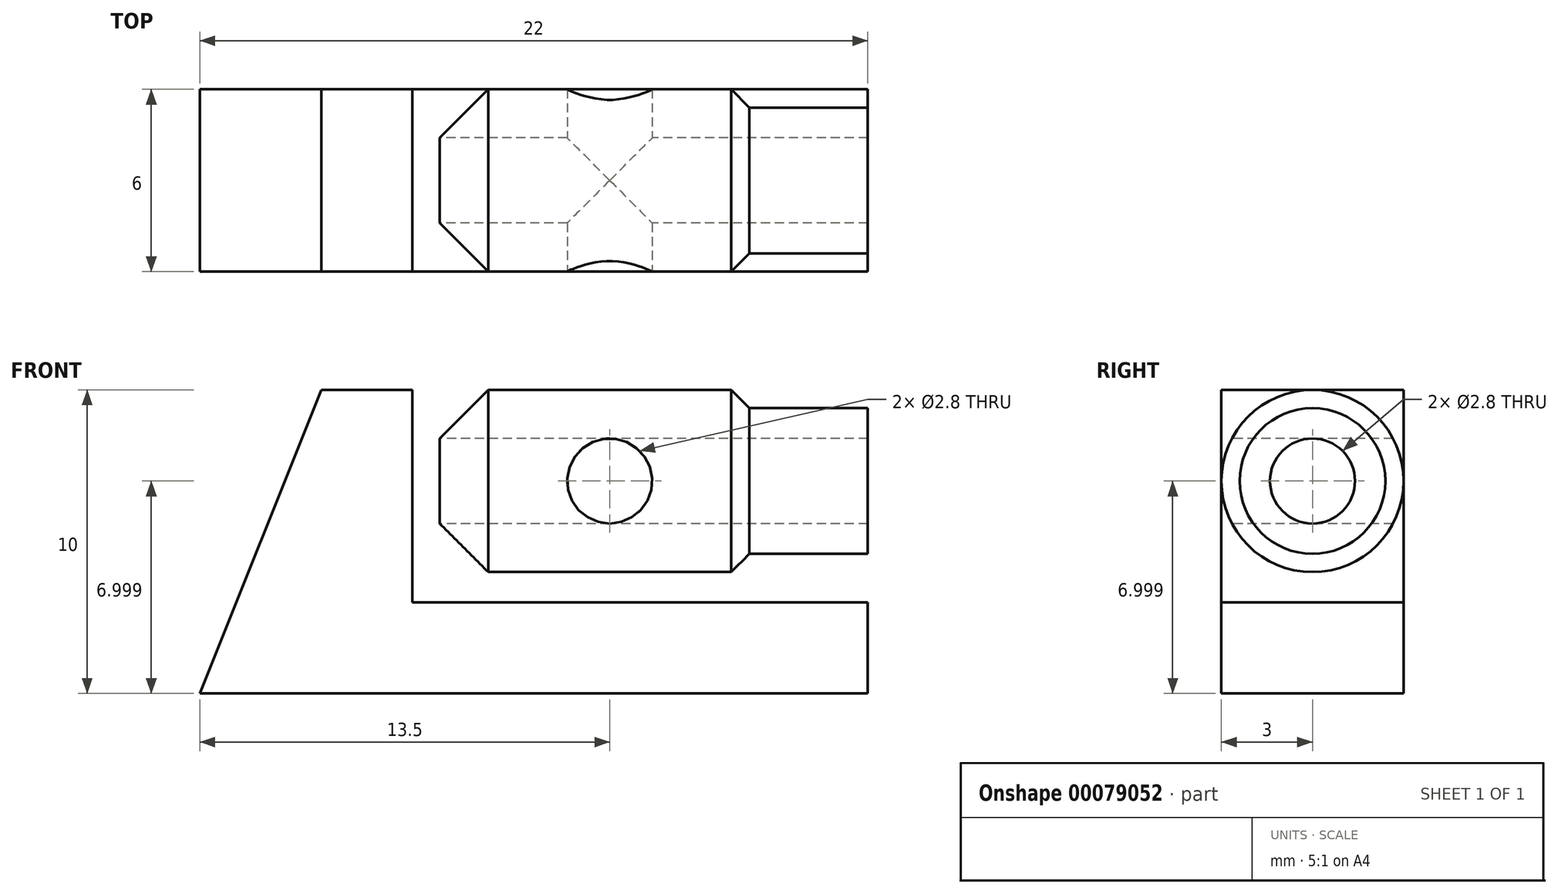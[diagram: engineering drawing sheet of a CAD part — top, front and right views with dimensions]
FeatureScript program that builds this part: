
annotation { "Feature Type Name" : "Feature", "Feature Type Description" : "" }
export const myFeature = defineFeature(function(context is Context, id is Id, definition is map)
    precondition{}
    {
        {
            var Q0;
            Q0=qCreatedBy(makeId("Front.planeOp"),FACE);
            var sketch = newSketch(context, id + "F0", { "sketchPlane" : qUnion([Q0])});
            skLineSegment(sketch, "E0", {"start": v(-15, 4.58) * mm, "end": v(0, 4.58) * mm});
            skLineSegment(sketch, "E1", {"start": v(0, 1.58) * mm, "end": v(-22, 1.58) * mm});
            skLineSegment(sketch, "E2", {"start": v(-22, 1.58) * mm, "end": v(-18, 11.58) * mm});
            skLineSegment(sketch, "E3", {"start": v(-18, 11.58) * mm, "end": v(-15, 11.58) * mm});
            skLineSegment(sketch, "E4", {"start": v(-15, 11.58) * mm, "end": v(-15, 4.58) * mm});
            skLineSegment(sketch, "E5", {"start": v(0, 4.58) * mm, "end": v(0, 1.58) * mm});
            skSolve(sketch);
        }
        {
            var Q0;
            Q0=makeQuery(id+"F0.imprint","IMPRINT",FACE,{"disambiguationData":[TD([[makeQuery(id+"F0.imprint","IMPRINT",EDGE,{"derivedFrom":sQuery(id+"F0.wireOp",EDGE,"E0")}),-1.0]])]});
            extrude(context, id + "F1", {"entities" : qUnion([Q0]), "depth" : 6 * mm});
        }
        {
            var Q0;
            Q0=makeQuery(id+"F1.opExtrude","SWEPT_FACE",FACE,{"disambiguationData":[OSD([sQuery(id+"F0.wireOp",EDGE,"E4")])]});
            var sketch = newSketch(context, id + "F2", { "sketchPlane" : qUnion([Q0])});
            skCircle(sketch, "E6", {"center": v(-3, 8.58) * mm, "radius": 1.4 * mm});
            skPoint(sketch, "E6.centerSnap0", {"position": v(-3, 11.58) * mm});
            skCircle(sketch, "E7", {"center": v(-3, 8.58) * mm, "radius": 3 * mm});
            skSolve(sketch);
        }
        {
            var Q0;
            Q0=makeQuery(id+"F2.imprint","IMPRINT",FACE,{"disambiguationData":[TD([[makeQuery(id+"F2.imprint","IMPRINT",EDGE,{"derivedFrom":sQuery(id+"F2.wireOp",EDGE,"E6")}),-1.0]])]});
            var Q1;
            Q1=makeQuery(id+"F1.opExtrude","SWEPT_FACE",FACE,{"disambiguationData":[OSD([sQuery(id+"F0.wireOp",EDGE,"E5")])]});
            extrude(context, id + "F3", {"entities" : qUnion([Q0]), "endBound" : BoundingType.UP_TO_SURFACE, "endBoundEntityFace" : qUnion([Q1]), "depth" : 25 * mm});
        }
        {
            var Q0;
            Q0=makeQuery(id+"F3.opExtrude","CAP_EDGE",EDGE,{"disambiguationData":[OSD([sQuery(id+"F2.wireOp",EDGE,"E7")])],"isStart":true});
            chamfer(context, id + "F4", {"entities" : qUnion([Q0]), "width" : 2.5 * mm, "tangentPropagation" : true});
        }
        {
            var Q0;
            Q0=makeQuery(id+"F1.opExtrude","CAP_FACE",FACE,{"disambiguationData":[OSD([sQuery(id+"F0.wireOp",EDGE,"E0"),sQuery(id+"F0.wireOp",EDGE,"E1"),sQuery(id+"F0.wireOp",EDGE,"E2"),sQuery(id+"F0.wireOp",EDGE,"E3"),sQuery(id+"F0.wireOp",EDGE,"E4"),sQuery(id+"F0.wireOp",EDGE,"E5")])],"isStart":false});
            var sketch = newSketch(context, id + "F5", { "sketchPlane" : qUnion([Q0])});
            skCircle(sketch, "E8", {"center": v(-8.5, 8.58) * mm, "radius": 1.4 * mm});
            skPoint(sketch, "E8.centerSnap0", {"position": v(-15, 8.58) * mm});
            skLineSegment(sketch, "E9.0", {"start": v(-12.5, 11.58) * mm, "end": v(-12.5, 5.58) * mm, "construction": true});
            skPoint(sketch, "E10", {"position": v(-12.5, 8.58) * mm});
            skSolve(sketch);
        }
        {
            var Q0;
            Q0=makeQuery(id+"F5.imprint","IMPRINT",FACE,{"disambiguationData":[TD([[makeQuery(id+"F5.imprint","IMPRINT",EDGE,{"derivedFrom":sQuery(id+"F5.wireOp",EDGE,"E8")}),1.0]])]});
            extrude(context, id + "F6", {"entities" : qUnion([Q0]), "operationType" : NewBodyOperationType.REMOVE, "oppositeDirection" : true, "depth" : 25 * mm});
        }
        {
            var Q0;
            Q0=makeQuery(id+"F3.opExtrude","CAP_FACE",FACE,{"disambiguationData":[OSD([sQuery(id+"F2.wireOp",EDGE,"E6"),sQuery(id+"F2.wireOp",EDGE,"E7")])],"isStart":false});
            var sketch = newSketch(context, id + "F7", { "sketchPlane" : qUnion([Q0])});
            skCircle(sketch, "E11", {"center": v(-3, 8.58) * mm, "radius": 2.4 * mm});
            skSolve(sketch);
        }
        {
            var Q0;
            Q0=makeQuery(id+"F7.imprint","IMPRINT",FACE,{"disambiguationData":[TD([[makeQuery(id+"F7.imprint","IMPRINT",EDGE,{"derivedFrom":sQuery(id+"F7.wireOp",EDGE,"E11")}),-1.0]])]});
            extrude(context, id + "F8", {"entities" : qUnion([Q0]), "operationType" : NewBodyOperationType.REMOVE, "oppositeDirection" : true, "depth" : 4.5 * mm});
        }
        {
            var Q0;
            Q0=makeQuery(id+"F8.boolean.opBoolean","COPY",EDGE,{"derivedFrom":makeQuery(id+"F8.opExtrude","CAP_EDGE",EDGE,{"disambiguationData":[OSD([sQuery(id+"F7.wireOp",EDGE,"E11")])],"isStart":false})});
            chamfer(context, id + "F9", {"entities" : qUnion([Q0]), "width" : 0.6 * mm, "tangentPropagation" : true});
        }
    });
